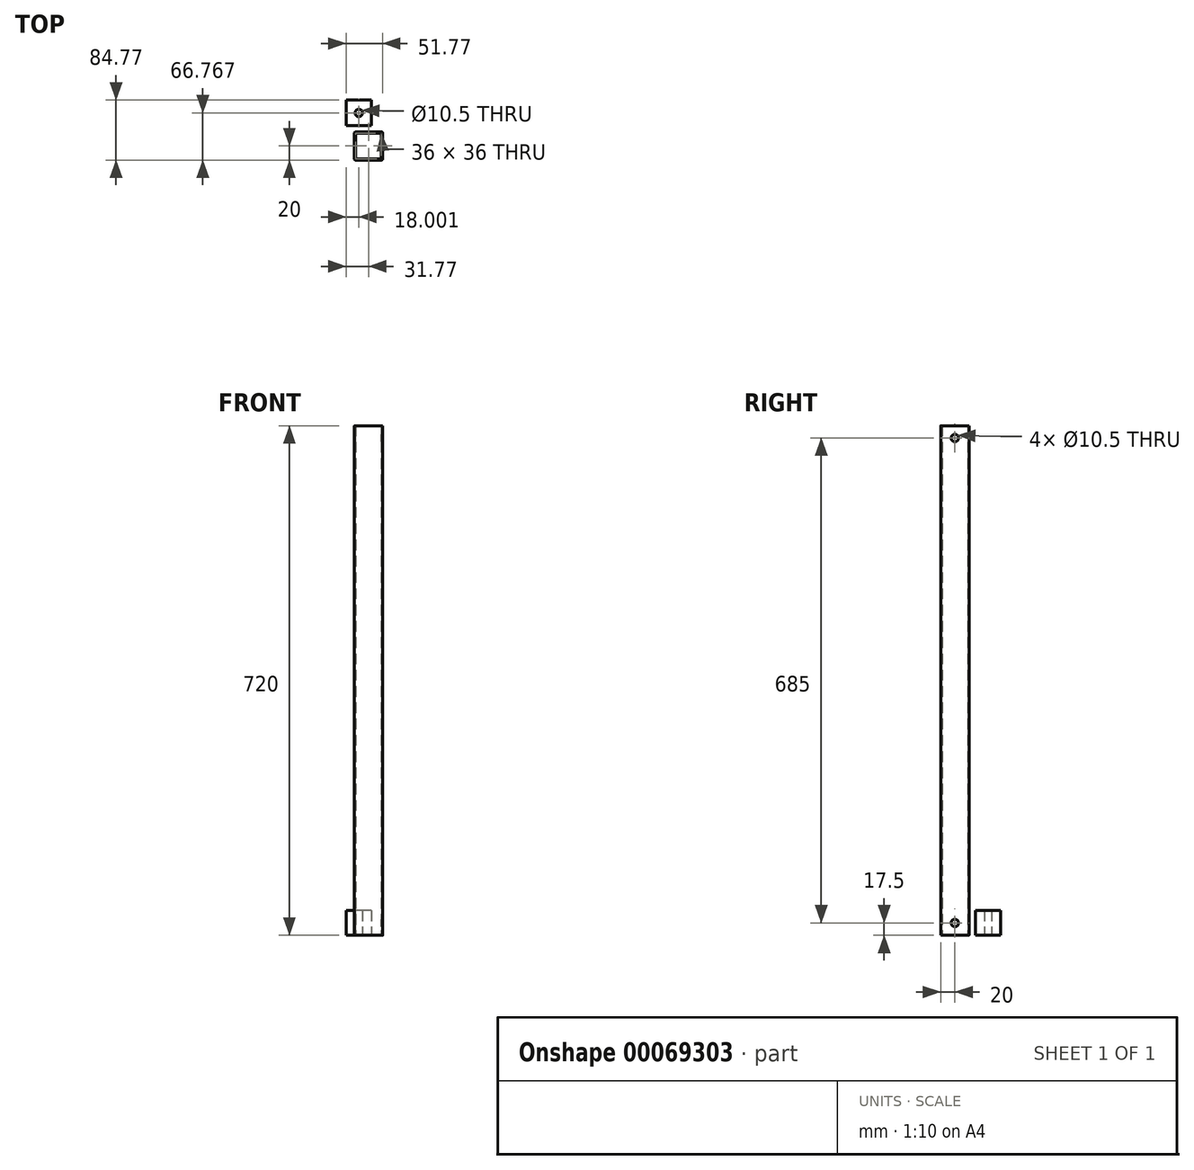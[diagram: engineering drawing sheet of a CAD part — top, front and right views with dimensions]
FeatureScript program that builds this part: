
annotation { "Feature Type Name" : "Feature", "Feature Type Description" : "" }
export const myFeature = defineFeature(function(context is Context, id is Id, definition is map)
    precondition{}
    {
        {
            var Q0;
            Q0=qCreatedBy(makeId("Top.planeOp"),FACE);
            var sketch = newSketch(context, id + "F0", { "sketchPlane" : qUnion([Q0])});
            skLineSegment(sketch, "E0.bottom", {"start": v(0, 0) * mm, "end": v(-40, 0) * mm});
            skLineSegment(sketch, "E0.top", {"start": v(0, -40) * mm, "end": v(-40, -40) * mm});
            skLineSegment(sketch, "E0.left", {"start": v(0, 0) * mm, "end": v(0, -40) * mm});
            skLineSegment(sketch, "E0.right", {"start": v(-40, 0) * mm, "end": v(-40, -40) * mm});
            skLineSegment(sketch, "E1.0", {"start": v(-2, -2) * mm, "end": v(-38, -2) * mm});
            skLineSegment(sketch, "E1.1", {"start": v(-2, -2) * mm, "end": v(-2, -38) * mm});
            skLineSegment(sketch, "E1.2", {"start": v(-2, -38) * mm, "end": v(-38, -38) * mm});
            skLineSegment(sketch, "E1.3", {"start": v(-38, -2) * mm, "end": v(-38, -38) * mm});
            skSolve(sketch);
        }
        {
            var Q0;
            Q0=qSketchRegion(id+"F0",true);
            extrude(context, id + "F1", {"entities" : qUnion([Q0]), "depth" : 720 * mm});
        }
        {
            var Q0;
            Q0=qCreatedBy(makeId("Top.planeOp"),FACE);
            var sketch = newSketch(context, id + "F2", { "sketchPlane" : qUnion([Q0])});
            skLineSegment(sketch, "E2.bottom", {"start": v(-15.77, 8.77) * mm, "end": v(-51.77, 8.77) * mm});
            skLineSegment(sketch, "E2.top", {"start": v(-15.77, 44.77) * mm, "end": v(-51.77, 44.77) * mm});
            skLineSegment(sketch, "E2.left", {"start": v(-15.77, 8.77) * mm, "end": v(-15.77, 44.77) * mm});
            skLineSegment(sketch, "E2.right", {"start": v(-51.77, 8.77) * mm, "end": v(-51.77, 44.77) * mm});
            skCircle(sketch, "E3", {"center": v(-33.77, 26.77) * mm, "radius": 5.25 * mm});
            skPoint(sketch, "E3.centerSnap0", {"position": v(-51.77, 26.77) * mm});
            skPoint(sketch, "E3.centerSnap1", {"position": v(-33.77, 8.77) * mm});
            skSolve(sketch);
        }
        {
            var Q0;
            Q0=qSketchRegion(id+"F2",true);
            extrude(context, id + "F3", {"entities" : qUnion([Q0]), "depth" : 35 * mm});
        }
        {
            var Q0;
            Q0=makeQuery(id+"F1.opExtrude","SWEPT_FACE",FACE,{"disambiguationData":[OSD([sQuery(id+"F0.wireOp",EDGE,"E0.right")])]});
            var sketch = newSketch(context, id + "F4", { "sketchPlane" : qUnion([Q0])});
            skLineSegment(sketch, "E4", {"start": v(40, 0) * mm, "end": v(0, 0) * mm});
            skLineSegment(sketch, "E5", {"start": v(40, 17.5) * mm, "end": v(0, 17.5) * mm});
            skCircle(sketch, "E6", {"center": v(20, 17.5) * mm, "radius": 5.25 * mm});
            skSolve(sketch);
        }
        {
            var Q0;
            Q0=sQuery(id+"F4.wireOp",VERTEX,"E6.center");
            var Q1;
            Q1=makeQuery(id+"F1.opExtrude","SWEPT_BODY",BODY,{"disambiguationData":[OSD([sQuery(id+"F0.wireOp",EDGE,"E0.bottom"),sQuery(id+"F0.wireOp",EDGE,"E0.top"),sQuery(id+"F0.wireOp",EDGE,"E0.left"),sQuery(id+"F0.wireOp",EDGE,"E0.right"),sQuery(id+"F0.wireOp",EDGE,"E1.0"),sQuery(id+"F0.wireOp",EDGE,"E1.1"),sQuery(id+"F0.wireOp",EDGE,"E1.2"),sQuery(id+"F0.wireOp",EDGE,"E1.3")])]});
            hole(context, id + "F5", {"style" : HoleStyle.SIMPLE, "holeDiameter" : 10.5 * mm, "endStyle" : HoleEndStyle.THROUGH, "locations" : qUnion([Q0]), "scope" : qUnion([Q1])});
        }
        {
            var Q0;
            Q0=makeQuery(id+"F1.opExtrude","SWEPT_FACE",FACE,{"disambiguationData":[OSD([sQuery(id+"F0.wireOp",EDGE,"E0.right")])]});
            var sketch = newSketch(context, id + "F6", { "sketchPlane" : qUnion([Q0])});
            skLineSegment(sketch, "E7", {"start": v(40, 720) * mm, "end": v(0, 720) * mm});
            skLineSegment(sketch, "E8", {"start": v(40, 702.5) * mm, "end": v(0, 702.5) * mm});
            skCircle(sketch, "E9", {"center": v(20, 702.5) * mm, "radius": 5.25 * mm});
            skSolve(sketch);
        }
        {
            var Q0;
            Q0=sQuery(id+"F6.wireOp",VERTEX,"E9.center");
            var Q1;
            Q1=makeQuery(id+"F1.opExtrude","SWEPT_BODY",BODY,{"disambiguationData":[OSD([sQuery(id+"F0.wireOp",EDGE,"E0.bottom"),sQuery(id+"F0.wireOp",EDGE,"E0.top"),sQuery(id+"F0.wireOp",EDGE,"E0.left"),sQuery(id+"F0.wireOp",EDGE,"E0.right"),sQuery(id+"F0.wireOp",EDGE,"E1.0"),sQuery(id+"F0.wireOp",EDGE,"E1.1"),sQuery(id+"F0.wireOp",EDGE,"E1.2"),sQuery(id+"F0.wireOp",EDGE,"E1.3")])]});
            hole(context, id + "F7", {"style" : HoleStyle.SIMPLE, "holeDiameter" : 10.5 * mm, "endStyle" : HoleEndStyle.THROUGH, "locations" : qUnion([Q0]), "scope" : qUnion([Q1])});
        }
        {
            var Q0;
            Q0=makeQuery(id+"F1.opExtrude","SWEPT_EDGE",EDGE,{"disambiguationData":[OSD([sQuery(id+"F0.wireOp",EDGE,"E0.top"),sQuery(id+"F0.wireOp",EDGE,"E0.left")])]});
            var Q1;
            Q1=makeQuery(id+"F1.opExtrude","SWEPT_EDGE",EDGE,{"disambiguationData":[OSD([sQuery(id+"F0.wireOp",EDGE,"E0.bottom"),sQuery(id+"F0.wireOp",EDGE,"E0.left")])]});
            var Q2;
            Q2=makeQuery(id+"F1.opExtrude","SWEPT_EDGE",EDGE,{"disambiguationData":[OSD([sQuery(id+"F0.wireOp",EDGE,"E0.top"),sQuery(id+"F0.wireOp",EDGE,"E0.right")])]});
            var Q3;
            Q3=makeQuery(id+"F1.opExtrude","SWEPT_EDGE",EDGE,{"disambiguationData":[OSD([sQuery(id+"F0.wireOp",EDGE,"E0.bottom"),sQuery(id+"F0.wireOp",EDGE,"E0.right")])]});
            fillet(context, id + "F8", {"entities" : qUnion([Q0, Q1, Q2, Q3]), "radius" : 2 * mm, "tangentPropagation" : true, "allowEdgeOverflow" : false});
        }
    });
